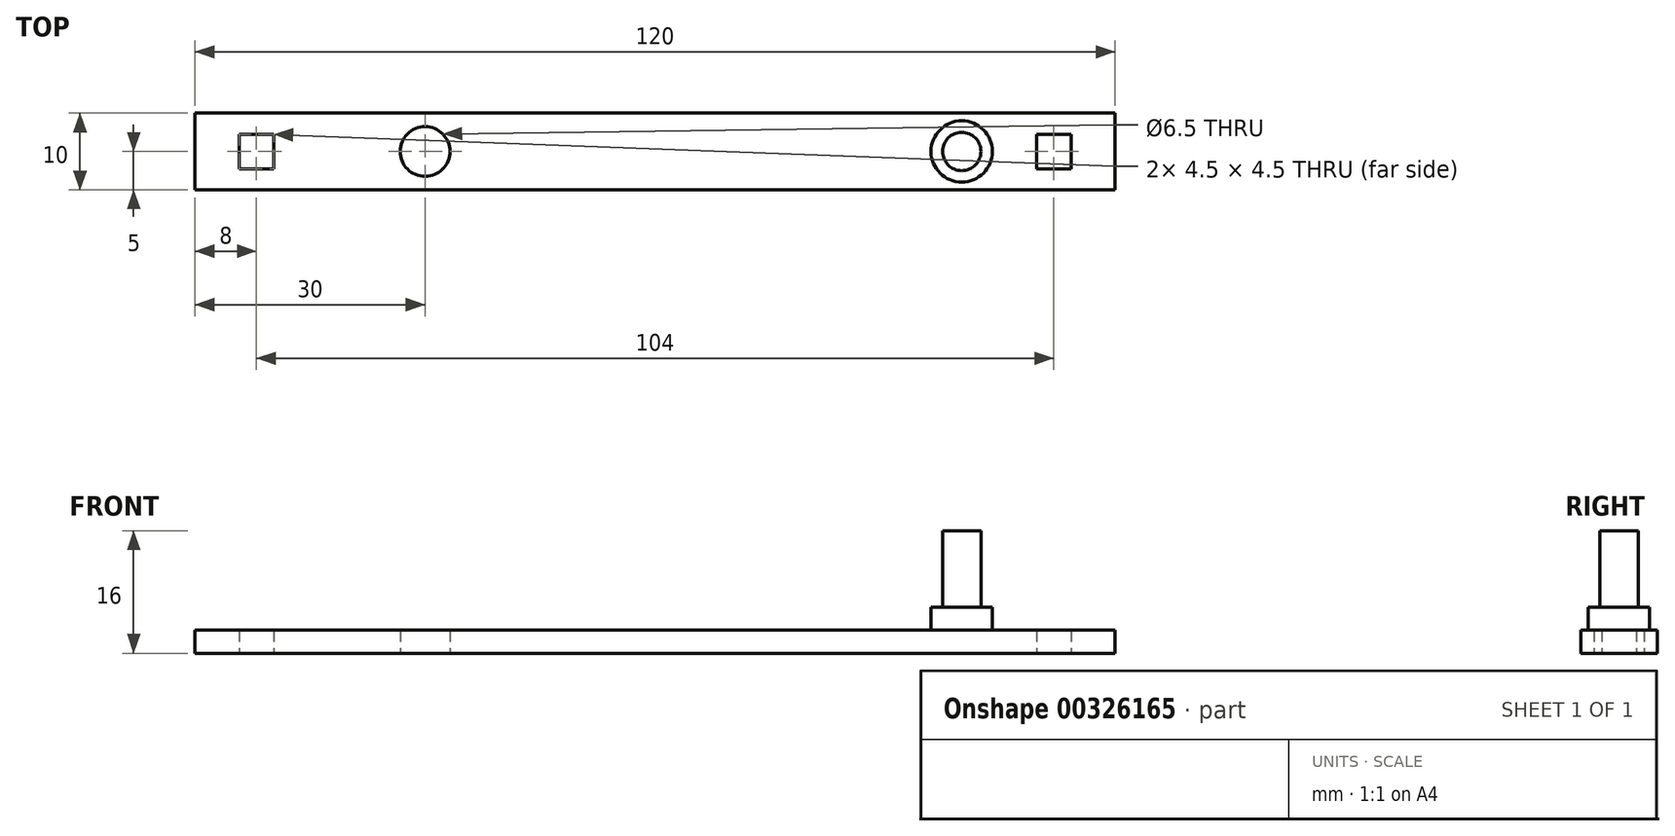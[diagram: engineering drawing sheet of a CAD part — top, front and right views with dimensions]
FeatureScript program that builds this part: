
annotation { "Feature Type Name" : "Feature", "Feature Type Description" : "" }
export const myFeature = defineFeature(function(context is Context, id is Id, definition is map)
    precondition{}
    {
        {
            var Q0;
            Q0=qCreatedBy(makeId("Top.planeOp"),FACE);
            var sketch = newSketch(context, id + "F0", { "sketchPlane" : qUnion([Q0])});
            skLineSegment(sketch, "E0.bottom", {"start": v(-60, 5) * mm, "end": v(60, 5) * mm});
            skLineSegment(sketch, "E0.top", {"start": v(-60, -5) * mm, "end": v(60, -5) * mm});
            skLineSegment(sketch, "E0.left", {"start": v(-60, 5) * mm, "end": v(-60, -5) * mm});
            skLineSegment(sketch, "E0.right", {"start": v(60, 5) * mm, "end": v(60, -5) * mm});
            skPoint(sketch, "E0.middle", {"position": v(0, 0) * mm});
            skLineSegment(sketch, "E1", {"start": v(0, 0) * mm, "end": v(-60, 0) * mm, "construction": true});
            skCircle(sketch, "E2", {"center": v(-30, 0) * mm, "radius": 3.25 * mm});
            skLineSegment(sketch, "E3", {"start": v(0, 0) * mm, "end": v(60, 0) * mm, "construction": true});
            skLineSegment(sketch, "E4.bottom", {"start": v(49.75, 2.25) * mm, "end": v(54.25, 2.25) * mm});
            skLineSegment(sketch, "E4.top", {"start": v(49.75, -2.25) * mm, "end": v(54.25, -2.25) * mm});
            skLineSegment(sketch, "E4.left", {"start": v(49.75, 2.25) * mm, "end": v(49.75, -2.25) * mm});
            skLineSegment(sketch, "E4.right", {"start": v(54.25, 2.25) * mm, "end": v(54.25, -2.25) * mm});
            skPoint(sketch, "E4.middle", {"position": v(52, 0) * mm});
            skLineSegment(sketch, "E5", {"start": v(0, 0) * mm, "end": v(0, 35.74) * mm, "construction": true});
            skPoint(sketch, "E5.endSnap0", {"position": v(0, 5) * mm});
            skLineSegment(sketch, "E6.MirrorCS", {"start": v(-54.25, 2.25) * mm, "end": v(-54.25, -2.25) * mm});
            skLineSegment(sketch, "E7.MirrorCS", {"start": v(-49.75, 2.25) * mm, "end": v(-54.25, 2.25) * mm});
            skLineSegment(sketch, "E8.MirrorCS", {"start": v(-49.75, 2.25) * mm, "end": v(-49.75, -2.25) * mm});
            skLineSegment(sketch, "E9.MirrorCS", {"start": v(-49.75, -2.25) * mm, "end": v(-54.25, -2.25) * mm});
            skSolve(sketch);
        }
        {
            var Q0;
            Q0 = qSketchRegion(id + "F0", true);
            extrude(context, id + "F1", {"entities" : qUnion([Q0]), "depth" : 3 * mm});
        }
        {
            var Q0;
            Q0=makeQuery(id+"F1.opExtrude","CAP_FACE",FACE,{"disambiguationData":[OSD([sQuery(id+"F0.wireOp",EDGE,"E0.bottom"),sQuery(id+"F0.wireOp",EDGE,"E0.top"),sQuery(id+"F0.wireOp",EDGE,"E0.left"),sQuery(id+"F0.wireOp",EDGE,"E0.right"),sQuery(id+"F0.wireOp",EDGE,"E2")])],"isStart":false});
            var sketch = newSketch(context, id + "F2", { "sketchPlane" : qUnion([Q0])});
            skLineSegment(sketch, "E10", {"start": v(0, 0) * mm, "end": v(60, 0) * mm, "construction": true});
            skCircle(sketch, "E11", {"center": v(40, 0) * mm, "radius": 4 * mm});
            skSolve(sketch);
        }
        {
            var Q0;
            Q0 = qSketchRegion(id + "F2", true);
            extrude(context, id + "F3", {"entities" : qUnion([Q0]), "operationType" : NewBodyOperationType.ADD, "depth" : 3 * mm});
        }
        {
            var Q0;
            Q0=makeQuery(id+"F3.opExtrude","CAP_FACE",FACE,{"disambiguationData":[OSD([sQuery(id+"F2.wireOp",EDGE,"E11")])],"isStart":false});
            var sketch = newSketch(context, id + "F4", { "sketchPlane" : qUnion([Q0])});
            skCircle(sketch, "E12.0", {"center": v(40, 0) * mm, "radius": 4 * mm, "construction": true});
            skCircle(sketch, "E13", {"center": v(40, 0) * mm, "radius": 2.5 * mm});
            skSolve(sketch);
        }
        {
            var Q0;
            Q0 = qSketchRegion(id + "F4", true);
            extrude(context, id + "F5", {"entities" : qUnion([Q0]), "operationType" : NewBodyOperationType.ADD, "depth" : 10 * mm});
        }
    });
